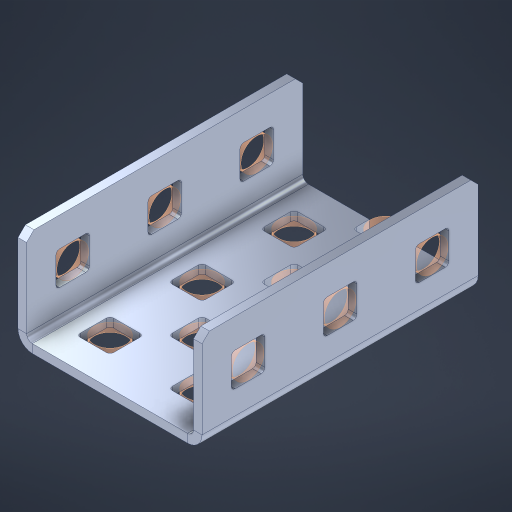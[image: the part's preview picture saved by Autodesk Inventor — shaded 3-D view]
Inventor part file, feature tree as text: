
AUTODESK INVENTOR PART (.ipt)
format: ipt  version: 2023 (Build 270158000, 158)  size: 549,888 bytes
history: native  units: in
note: dims shown in document units (in); Inventor stores cm internally (conversion verified against a paired STEP export)
features: other x22, extrude x13, sheet_metal_op x11, sketch x10, pattern_linear x2, mirror x1, chamfer x1
ambient origin geometry x8: Origin, YZ Plane, XZ Plane, XY Plane, X Axis, Y Axis, Z Axis, Center Point
bodies: Solid1 (feature_tree), Body (feature_tree)
feature tree (60):
  sheet_metal_op  "Flanges"
  other  "Flange Pattern Plane"
  other  "Flange Pattern Sketch"
  sheet_metal_op  "Flange Pattern"
  sheet_metal_op  "Body Pattern"
  pattern_linear  "Center Pattern"  Spacing1=0.0469in  [1 undecoded]
  other  "Arc Length"
  mirror  "Notch Mirror"
  pattern_linear  "Notch Pattern"  Spacing1=0.182in  [1 undecoded]
  chamfer  "End Chamfer"
  extrude  "Half Cut"  Depth=0.02in
  sketch  "Sketch1"  dims[d0=1.0in]
  other  "Plate1"
  sketch  "Sketch2"  dims[d1=1.5in]
  other  "Plate2"
  sheet_metal_op  "Bend1"
  sheet_metal_op  "Corner1"
  sketch  "Sketch3"  dims[d2=0.0469in]
  sketch  "Sketch7"  dims[d3=0.0469in]
  other  "Srf1"
  other  "Srf2"
  sketch  "Sketch8"  dims[d4=0.0234in]
  sketch  "Sketch9"  dims[d5=0.0938in]
  other  "Srf91"
  sheet_metal_op  "Body Pattern Sketch"
  other  "Srf92"
  sketch  "Sketch13"  dims[d6=0.0469in]
  sketch  "Sketch14"  dims[d7=0.5in d8=90.0deg d9=0.0312in]
  sketch  "Sketch15"  dims[d10=0.1875in]
  sketch  "Sketch16"  dims[d11=0.0469in d12=0.0469in d16=0.182in d17=0.02in d18=0.0469in d19=0.0in d20=0.25in d21=0.25in d38=1.1811in d40=0.5in d41=0.7874in d43=1.0in d46=0.172in d47=1.0in d48=0.0in d49=0.182in d50=0.02in d51=0.25in d52=0.25in d53=0.0469in d54=0.0in d55=0.172in d56=1.0in d57=0.0in d58=0.25in d60=1.1811in d62=0.5in d63=0.7874in d65=0.5in d85=0.1227in d86=0.1659in d88=0.04in d89=0.0469in d90=0.0in d91=0.04in d92=0.0491in d95=2.5in d96=0.04in d97=0.25in d98=45.0deg d99=0.25in d100=0.5in d101=0.0in d102=2.497in d106=0.182in d107=0.02in d108=0.5in d109=0.5in d110=0.0469in d111=0.0in d112=0.172in d113=0.5in d114=0.0in d117=0.5in d118=0.5in d119=0.5in]
  other  "Srf786"
  other  "Srf823"
  other  "Srf824"
  other  "Srf825"
  other  "Srf826"
  other  "Srf856"
  other  "Srf857"
  other  "Srf858"
  other  "Srf859"
  other  "Srf889"
  other  "Srf890"
  sheet_metal_op  "Flange Stamp"
  sheet_metal_op  "Flange Circle"
  sheet_metal_op  "Body Stamp"
  sheet_metal_op  "Body Circle"
  other  "Center Stamp"
  other  "Center Circle"
  sheet_metal_op  "Notch"
  extrude  "ExtrusionSrf2"  Depth=0.0469in
  extrude  "ExtrusionSrf92"  TaperAngle=0.0deg  [1 undecoded]
  extrude  "ExtrusionSrf823"  Depth=0.25in
  extrude  "ExtrusionSrf824"  Depth=0.25in
  extrude  "ExtrusionSrf825"  Depth=0.5in
  extrude  "ExtrusionSrf826"  Depth=0.5in
  extrude  "ExtrusionSrf856"  Depth=1.0in TaperAngle=0.0deg
  extrude  "ExtrusionSrf857"  Depth=0.182in
  extrude  "ExtrusionSrf858"  Depth=0.02in
  extrude  "ExtrusionSrf859"  Depth=0.25in
  extrude  "ExtrusionSrf889"  Depth=0.25in
  extrude  "ExtrusionSrf890"  Depth=0.0469in
note: 3 required parameter values undecoded (feature->parameter linkage not recoverable at this tier; creation-order binding heuristic only, values carry confidence <= 0.55)
